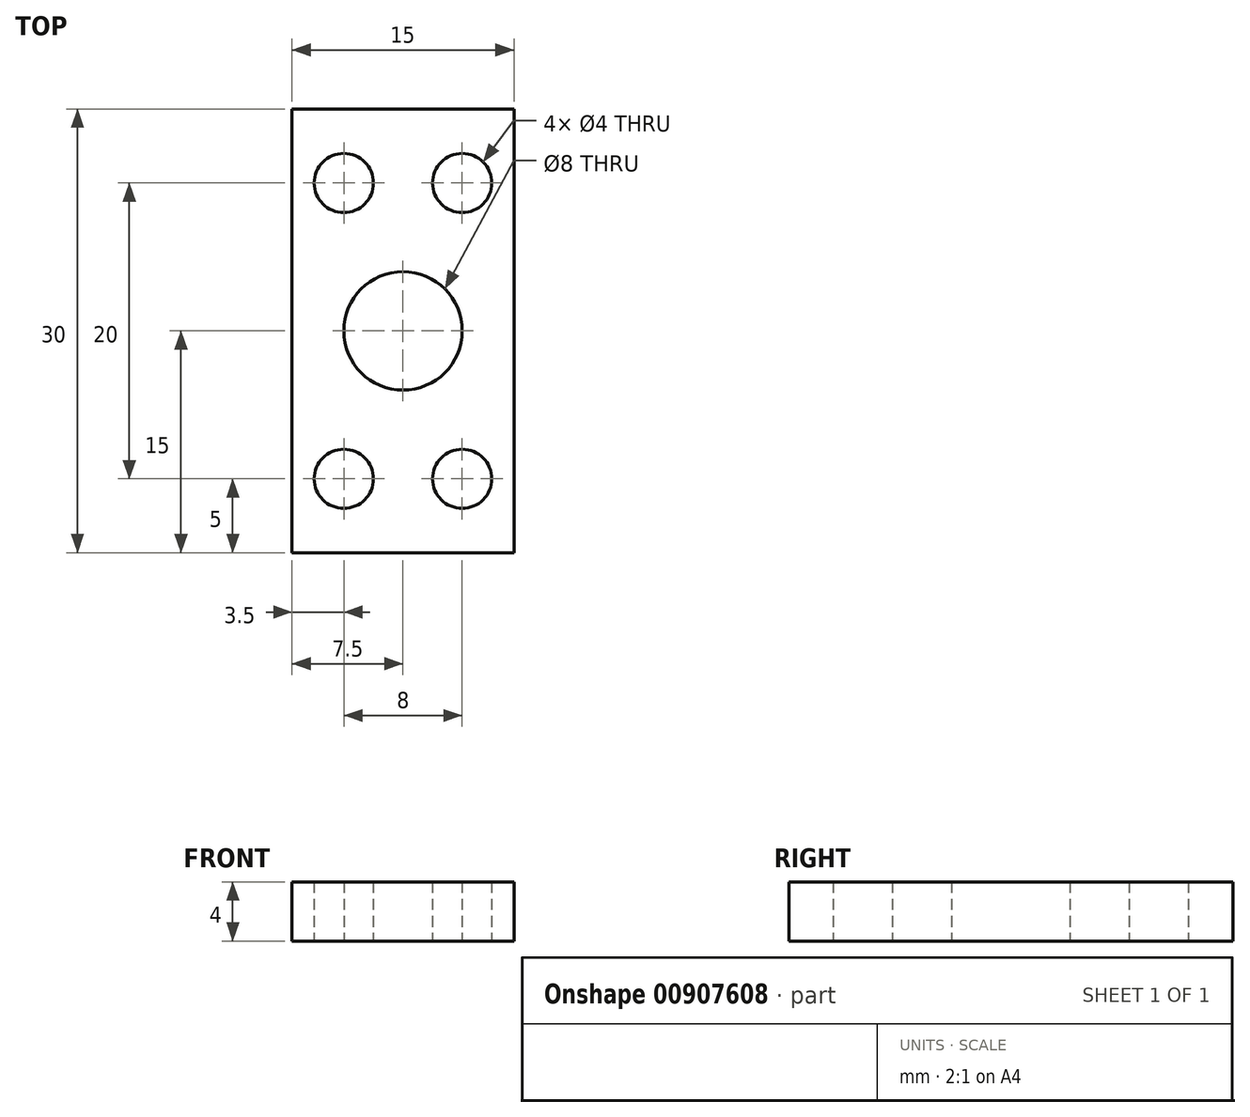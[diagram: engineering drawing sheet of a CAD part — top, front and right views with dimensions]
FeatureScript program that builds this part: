
annotation { "Feature Type Name" : "Feature", "Feature Type Description" : "" }
export const myFeature = defineFeature(function(context is Context, id is Id, definition is map)
    precondition{}
    {
        {
            var Q0;
            Q0=qCreatedBy(makeId("Top.planeOp"),FACE);
            var sketch = newSketch(context, id + "F0", { "sketchPlane" : qUnion([Q0])});
            skLineSegment(sketch, "E0.bottom", {"start": v(7.5, 15) * mm, "end": v(-7.5, 15) * mm});
            skLineSegment(sketch, "E0.top", {"start": v(7.5, -15) * mm, "end": v(-7.5, -15) * mm});
            skLineSegment(sketch, "E0.left", {"start": v(7.5, 15) * mm, "end": v(7.5, -15) * mm});
            skLineSegment(sketch, "E0.right", {"start": v(-7.5, 15) * mm, "end": v(-7.5, -15) * mm});
            skPoint(sketch, "E0.middle", {"position": v(0, 0) * mm});
            skLineSegment(sketch, "E1", {"start": v(0, 49.05) * mm, "end": v(0, -39.53) * mm, "construction": true});
            skLineSegment(sketch, "E2", {"start": v(-26.29, 0) * mm, "end": v(33.84, 0) * mm, "construction": true});
            skCircle(sketch, "E3", {"center": v(-4, 10) * mm, "radius": 2 * mm});
            skCircle(sketch, "E4.MirrorC", {"center": v(4, 10) * mm, "radius": 2 * mm});
            skLineSegment(sketch, "E5.MirrorCS", {"start": v(26.29, 0) * mm, "end": v(-33.84, 0) * mm, "construction": true});
            skCircle(sketch, "E6.MirrorC", {"center": v(-4, -10) * mm, "radius": 2 * mm});
            skCircle(sketch, "E7.MirrorC", {"center": v(4, -10) * mm, "radius": 2 * mm});
            skCircle(sketch, "E8", {"center": v(0, 0) * mm, "radius": 4 * mm});
            skSolve(sketch);
        }
        {
            var Q0;
            Q0=makeQuery(id+"F0.imprint","IMPRINT",FACE,{"disambiguationData":[TD([[makeQuery(id+"F0.imprint","IMPRINT",EDGE,{"derivedFrom":sQuery(id+"F0.wireOp",EDGE,"E0.bottom")}),1.0]])]});
            extrude(context, id + "F1", {"entities" : qUnion([Q0]), "depth" : 4 * mm, "offsetDistance" : 25 * mm});
        }
    });
